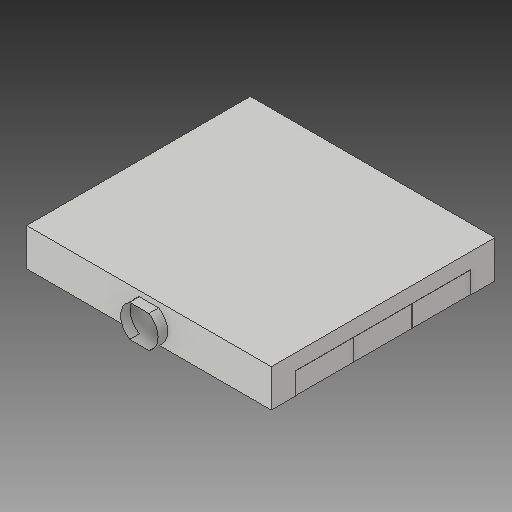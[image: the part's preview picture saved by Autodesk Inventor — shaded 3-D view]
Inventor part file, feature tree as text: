
AUTODESK INVENTOR PART (.ipt)
format: ipt  version: 2017 (Build 210142000, 142)  size: 293,888 bytes
history: native  units: in
note: dims shown in document units (in); Inventor stores cm internally (conversion verified against a paired STEP export)
features: extrude x6, sketch x4, delete_face x1
ambient origin geometry x8: Origin, YZ Plane, XZ Plane, XY Plane, X Axis, Y Axis, Z Axis, Center Point
bodies: Solid1 (feature_tree)
feature tree (11):
  extrude  "cubicals"  Depth=12.0in
  extrude  "floor"  Depth=2.5in
  extrude  "walls"  Depth=0.0833in
  extrude  "connection"  Depth=0.0833in
  extrude  "connection cut"  Depth=2.5in
  extrude  "ceiling"  Depth=2.5in
  delete_face  "Delete Face1"
  sketch  "Sketch2"  dims[d2=4.5in d3=0.0in d4=12.0in]
  sketch  "Sketch3"  dims[d5=8.0in d7=2.5in]
  sketch  "Sketch6"  dims[d10=0.0833in d95=0.0833in]
  sketch  "Sketch7"  dims[d97=0.0833in d98=0.0833in d99=12.0in d100=8.0in d102=0.0833in d103=0.0833in d104=0.0833in d105=0.0833in d106=12.0in d107=8.0in d109=0.0833in d110=0.0833in d111=0.0833in d112=0.0833in d113=2.5in d114=2.5in d115=3.0in d117=3.0in d118=6.0in d120=6.0in d121=1.0in d122=0.0in d128=1.0in d129=1.0in d130=1.0in d131=1.0in d132=1.0in d133=1.0in d134=7.7746in d135=0.0in d160=1.0in d161=0.0in d171=1.0in d172=0.0in d173=1.0in d174=0.0in d175=4.0in d177=3.8873in d178=3.8873in d182=1.6458in d187=3.3333in d188=1.0in d189=1.0in]
